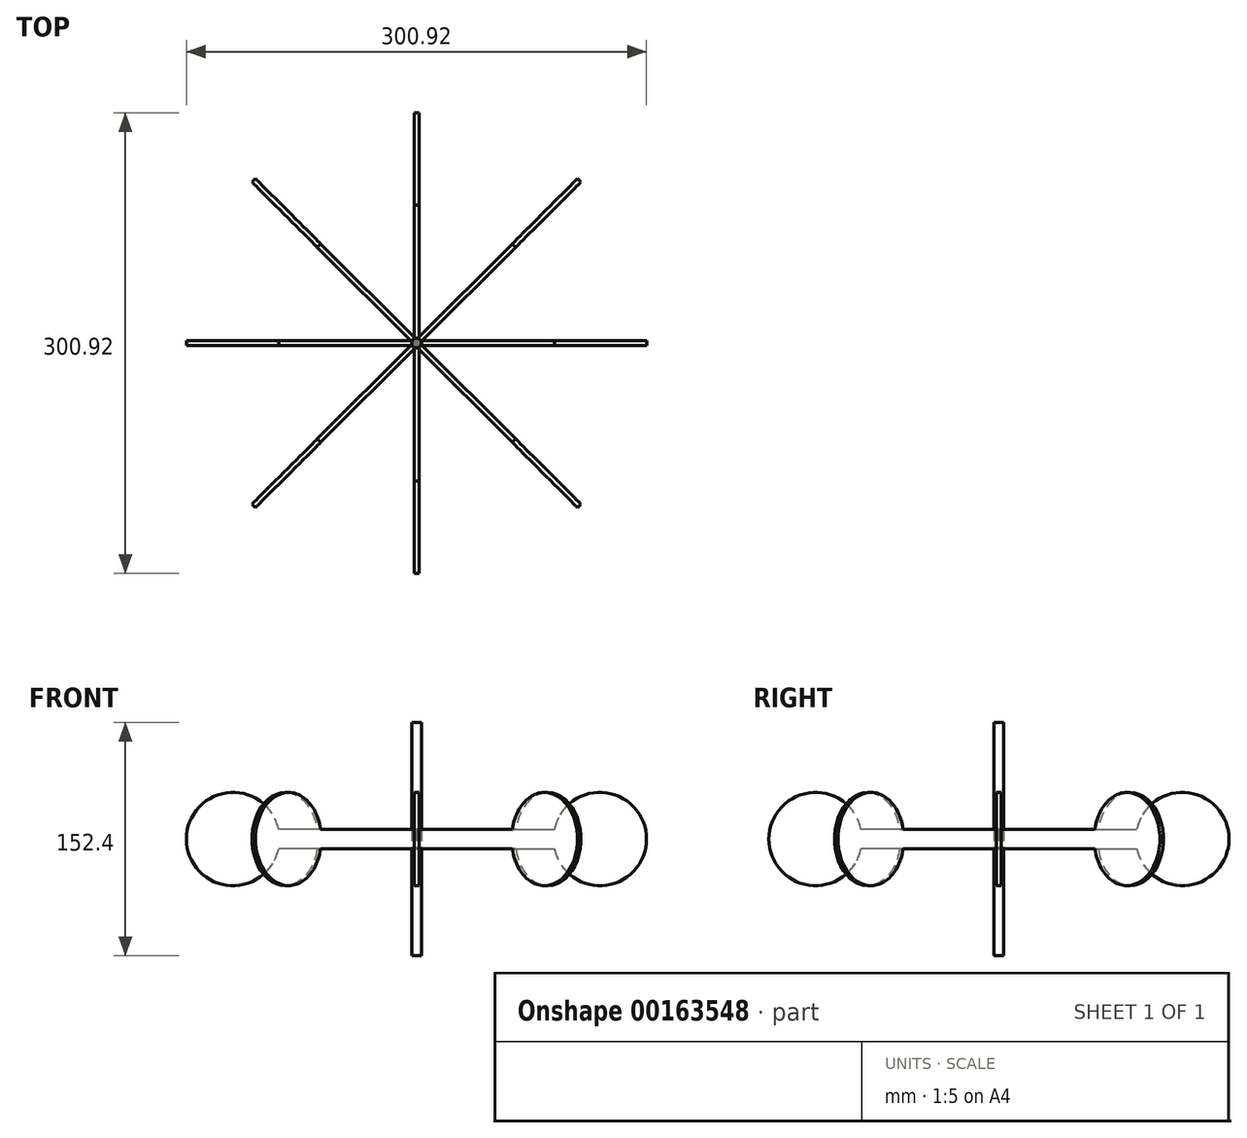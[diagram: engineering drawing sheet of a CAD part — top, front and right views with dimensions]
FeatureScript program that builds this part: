
annotation { "Feature Type Name" : "Feature", "Feature Type Description" : "" }
export const myFeature = defineFeature(function(context is Context, id is Id, definition is map)
    precondition{}
    {
        {
            var Q0;
            Q0=qCreatedBy(makeId("Front.planeOp"),FACE);
            var sketch = newSketch(context, id + "F0", { "sketchPlane" : qUnion([Q0])});
            skLineSegment(sketch, "E0", {"start": v(0, 6.35) * mm, "end": v(90.17, 6.35) * mm});
            skLineSegment(sketch, "E1.MirrorCS", {"start": v(0, -6.35) * mm, "end": v(90.17, -6.35) * mm});
            skArc(sketch, "E2", {"start": v(90.17, -6.35) * mm, "mid": v(150.46, 0) * mm, "end": v(90.17, 6.35) * mm});
            skLineSegment(sketch, "E3", {"start": v(0, 6.35) * mm, "end": v(0, -6.35) * mm});
            skSolve(sketch);
        }
        {
            var Q0;
            Q0 = qSketchRegion(id + "F0", true);
            extrude(context, id + "F1", {"entities" : qUnion([Q0]), "endBound" : BoundingType.SYMMETRIC, "depth" : 3.17 * mm});
        }
        {
            var Q0;
            Q0=qCreatedBy(makeId("Top.planeOp"),FACE);
            var sketch = newSketch(context, id + "F2", { "sketchPlane" : qUnion([Q0])});
            skCircle(sketch, "E4", {"center": v(0, 0) * mm, "radius": 3.18 * mm});
            skSolve(sketch);
        }
        {
            var Q0;
            Q0 = qSketchRegion(id + "F2", true);
            extrude(context, id + "F3", {"entities" : qUnion([Q0]), "endBound" : BoundingType.SYMMETRIC, "depth" : 152.4 * mm});
        }
        {
            var Q0;
            Q0=makeQuery(id+"F1.opExtrude","SWEPT_BODY",BODY,{"disambiguationData":[OSD([sQuery(id+"F0.wireOp",EDGE,"E0"),sQuery(id+"F0.wireOp",EDGE,"E1.MirrorCS"),sQuery(id+"F0.wireOp",EDGE,"E2"),sQuery(id+"F0.wireOp",EDGE,"E3")])]});
            var Q1;
            Q1=makeQuery(id+"F3.opExtrude","SWEPT_FACE",FACE,{"disambiguationData":[OSD([sQuery(id+"F2.wireOp",EDGE,"E4")])]});
            circularPattern(context, id + "F4", {"entities" : qUnion([Q0]), "axis" : qUnion([Q1]), "angle" : 45 * degree, "instanceCount" : 8});
        }
    });
